# Revit family: anti-flooding valve Stausafe E DN 150
name_source: partatom
category: Příslušenství trubek
revit_build: Autodesk Revit 2016 (Build: 20161004_0715(x64)
units: mm (PartAtom-declared; Revit-internal decimal feet)

## family parameters
Kóta kulaté spojky = Použít průměr
Ořezat dutým tvarem při načtení = Ne
Sdílené = Ne
Typ součásti = Připojí se k
Vždy vertikální = Ano
Založené na pracovní rovině = Ne

## types (1)
- anti-flooding valve Stausafe E DN 150
    Cena = 0 $
    DIMENSION = DN 150
    GTIN = 4001636661098
    Klíčová poznámka = Anti-flooding valve Stausafe E, DN 150
    Komentáře k typům = self-closing stainless steel flap, stainless steel pivots, easy to maintain ABS housing, inspection cover with wingnuts can be opened for maintenance without tools
    MATERIAL = ABS, stainless steel, plastic
    Model = Anti-flooding valve Stausafe E, DN 150
    NOMINAL DIAMETER = 150 mm
    NOMINAL DIAMETER 2 = 150 mm
    Popis = Anti-flooding valve
    URL = https://www.dallmer.de
    Výrobce = Dallmer Ltd.
